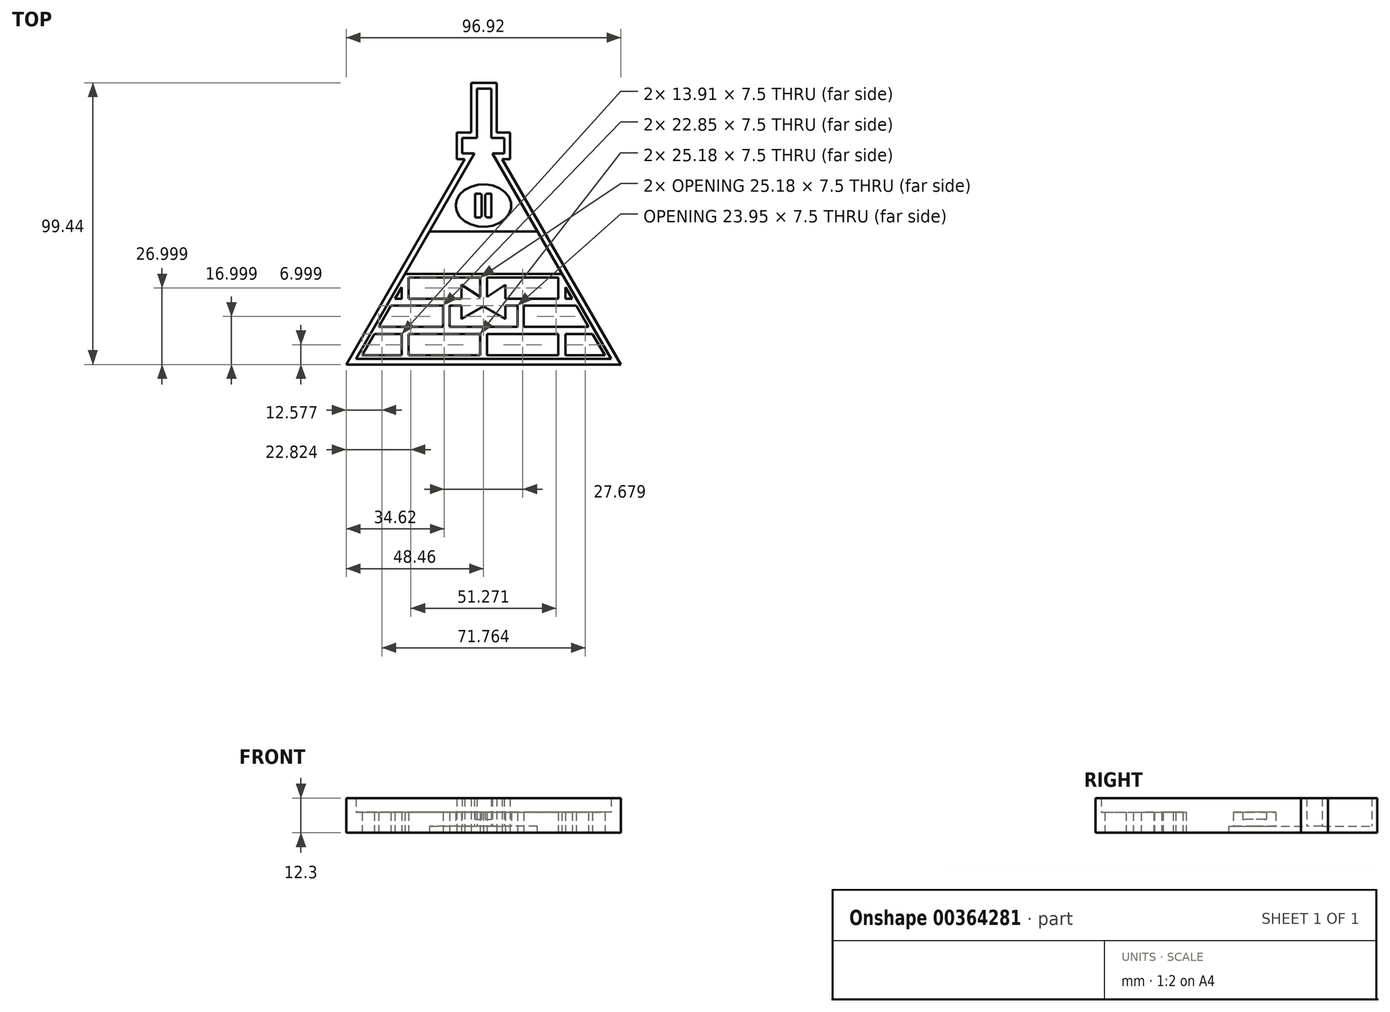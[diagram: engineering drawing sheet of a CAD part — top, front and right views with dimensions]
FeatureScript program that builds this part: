
annotation { "Feature Type Name" : "Feature", "Feature Type Description" : "" }
export const myFeature = defineFeature(function(context is Context, id is Id, definition is map)
    precondition{}
    {
        {
            var Q0;
            Q0=qCreatedBy(makeId("Top.planeOp"),FACE);
            var sketch = newSketch(context, id + "F0", { "sketchPlane" : qUnion([Q0])});
            skLineSegment(sketch, "E0", {"start": v(-13.53, -35.83) * mm, "end": v(31.47, -35.83) * mm});
            skLineSegment(sketch, "E1", {"start": v(31.47, -35.83) * mm, "end": v(-10.37, 36.64) * mm});
            skLineSegment(sketch, "E2", {"start": v(-13.53, 25.79) * mm, "end": v(-13.53, 10.79) * mm});
            skPoint(sketch, "E3.orphan", {"position": v(-58.53, -35.83) * mm});
            skEllipticalArc(sketch, "E4", {});
            skLineSegment(sketch, "E5", {"start": v(-13.53, -5.83) * mm, "end": v(14.15, -5.83) * mm});
            skLineSegment(sketch, "E6", {"start": v(-7.04, -15.83) * mm, "end": v(19.92, -15.83) * mm});
            skLineSegment(sketch, "E7", {"start": v(-13.53, -25.83) * mm, "end": v(25.7, -25.83) * mm});
            skLineSegment(sketch, "E8", {"start": v(14.15, -5.83) * mm, "end": v(14.15, -15.83) * mm});
            skLineSegment(sketch, "E9.trimOffspring", {"start": v(14.15, -25.83) * mm, "end": v(14.15, -35.83) * mm});
            skLineSegment(sketch, "E10", {"start": v(-0.57, -15.83) * mm, "end": v(-0.57, -25.83) * mm});
            skLineSegment(sketch, "E11", {"start": v(-12.28, -34.58) * mm, "end": v(-12.28, -27.08) * mm});
            skLineSegment(sketch, "E12", {"start": v(-12.28, -27.08) * mm, "end": v(12.9, -27.08) * mm});
            skLineSegment(sketch, "E13", {"start": v(12.9, -27.08) * mm, "end": v(12.9, -34.58) * mm});
            skLineSegment(sketch, "E14", {"start": v(12.9, -34.58) * mm, "end": v(-12.28, -34.58) * mm});
            skLineSegment(sketch, "E15", {"start": v(15.4, -34.58) * mm, "end": v(15.4, -27.08) * mm});
            skLineSegment(sketch, "E16", {"start": v(15.4, -27.08) * mm, "end": v(24.97, -27.08) * mm});
            skLineSegment(sketch, "E17", {"start": v(24.97, -27.08) * mm, "end": v(29.3, -34.58) * mm});
            skLineSegment(sketch, "E18", {"start": v(29.3, -34.58) * mm, "end": v(15.4, -34.58) * mm});
            skLineSegment(sketch, "E19", {"start": v(0.68, -24.58) * mm, "end": v(0.68, -17.08) * mm});
            skLineSegment(sketch, "E20", {"start": v(0.68, -17.08) * mm, "end": v(19.2, -17.08) * mm});
            skLineSegment(sketch, "E21", {"start": v(19.2, -17.08) * mm, "end": v(23.53, -24.58) * mm});
            skLineSegment(sketch, "E22", {"start": v(23.53, -24.58) * mm, "end": v(0.68, -24.58) * mm});
            skLineSegment(sketch, "E23", {"start": v(-1.56, -17.08) * mm, "end": v(-1.56, -24.58) * mm});
            skLineSegment(sketch, "E24", {"start": v(-12.28, -18) * mm, "end": v(-5.79, -21.75) * mm});
            skLineSegment(sketch, "E25", {"start": v(-5.79, -21.75) * mm, "end": v(-5.79, -17.08) * mm});
            skLineSegment(sketch, "E26", {"start": v(-5.79, -17.08) * mm, "end": v(-1.56, -17.08) * mm});
            skLineSegment(sketch, "E27", {"start": v(-12.28, -7.08) * mm, "end": v(-12.28, -14.01) * mm});
            skLineSegment(sketch, "E28", {"start": v(-12.28, -14.01) * mm, "end": v(-5.79, -9.6) * mm});
            skLineSegment(sketch, "E29", {"start": v(-5.79, -9.6) * mm, "end": v(-5.79, -14.58) * mm});
            skLineSegment(sketch, "E30", {"start": v(-5.79, -14.58) * mm, "end": v(12.9, -14.58) * mm});
            skLineSegment(sketch, "E31", {"start": v(12.9, -14.58) * mm, "end": v(12.9, -7.08) * mm});
            skLineSegment(sketch, "E32", {"start": v(12.9, -7.08) * mm, "end": v(-12.28, -7.08) * mm});
            skLineSegment(sketch, "E33", {"start": v(15.4, -14.58) * mm, "end": v(15.4, -10.5) * mm});
            skLineSegment(sketch, "E34", {"start": v(15.4, -10.5) * mm, "end": v(17.76, -14.58) * mm});
            skLineSegment(sketch, "E35", {"start": v(17.76, -14.58) * mm, "end": v(15.4, -14.58) * mm});
            skFitSpline(sketch, "E36.0", {"points": [v(-22.02, 19.44) * mm, v(-22.17, 18.29) * mm, v(-22.02, 17.13) * mm, v(-21.58, 16) * mm, v(-20.82, 14.92) * mm, v(-19.78, 13.95) * mm, v(-18.47, 13.13) * mm, v(-16.94, 12.5) * mm, v(-15.56, 12.19) * mm, v(-14.4, 12.06) * mm, v(-13.53, 12.03) * mm, v(-12.65, 12.06) * mm, v(-11.5, 12.19) * mm, v(-10.12, 12.5) * mm, v(-8.59, 13.13) * mm, v(-7.28, 13.95) * mm, v(-6.24, 14.92) * mm, v(-5.48, 16) * mm, v(-5.04, 17.13) * mm, v(-4.89, 18.29) * mm, v(-5.04, 19.44) * mm, v(-5.48, 20.56) * mm, v(-6.24, 21.65) * mm, v(-7.28, 22.62) * mm, v(-8.59, 23.44) * mm, v(-10.12, 24.06) * mm, v(-11.5, 24.38) * mm, v(-12.65, 24.51) * mm, v(-13.53, 24.55) * mm, v(-14.4, 24.51) * mm, v(-15.56, 24.38) * mm, v(-16.94, 24.06) * mm, v(-18.47, 23.44) * mm, v(-19.78, 22.62) * mm, v(-20.82, 21.65) * mm, v(-21.58, 20.56) * mm, v(-22.02, 19.44) * mm, v(-22.17, 18.29) * mm, v(-22.02, 17.13) * mm]});
            skEllipticalArc(sketch, "E37.MirrorCS", {});
            skLineSegment(sketch, "E38.MirrorCS", {"start": v(-58.53, -35.83) * mm, "end": v(-16.69, 36.64) * mm});
            skLineSegment(sketch, "E39.MirrorCS", {"start": v(-13.53, -5.83) * mm, "end": v(-41.21, -5.83) * mm});
            skLineSegment(sketch, "E40.MirrorCS", {"start": v(-39.96, -7.08) * mm, "end": v(-14.78, -7.08) * mm});
            skLineSegment(sketch, "E41.MirrorCS", {"start": v(-14.78, -7.08) * mm, "end": v(-14.78, -14.01) * mm});
            skLineSegment(sketch, "E42.MirrorCS", {"start": v(-14.78, -14.01) * mm, "end": v(-21.28, -9.6) * mm});
            skLineSegment(sketch, "E43.MirrorCS", {"start": v(-21.28, -17.08) * mm, "end": v(-25.5, -17.08) * mm});
            skLineSegment(sketch, "E44.MirrorCS", {"start": v(-21.28, -21.75) * mm, "end": v(-21.28, -17.08) * mm});
            skLineSegment(sketch, "E45.MirrorCS", {"start": v(-25.5, -17.08) * mm, "end": v(-25.5, -24.58) * mm});
            skLineSegment(sketch, "E46.MirrorCS", {"start": v(-14.78, -18) * mm, "end": v(-21.28, -21.75) * mm});
            skLineSegment(sketch, "E47.MirrorCS", {"start": v(-13.53, -25.83) * mm, "end": v(-52.76, -25.83) * mm});
            skLineSegment(sketch, "E48.MirrorCS", {"start": v(-27.74, -24.58) * mm, "end": v(-27.74, -17.08) * mm});
            skLineSegment(sketch, "E49.MirrorCS", {"start": v(-20.03, -15.83) * mm, "end": v(-46.98, -15.83) * mm});
            skLineSegment(sketch, "E50.MirrorCS", {"start": v(-26.5, -15.83) * mm, "end": v(-26.5, -25.83) * mm});
            skLineSegment(sketch, "E51.MirrorCS", {"start": v(-39.96, -14.58) * mm, "end": v(-39.96, -7.08) * mm});
            skLineSegment(sketch, "E52.MirrorCS", {"start": v(-46.26, -17.08) * mm, "end": v(-50.6, -24.58) * mm});
            skLineSegment(sketch, "E53.MirrorCS", {"start": v(-52.04, -27.08) * mm, "end": v(-56.37, -34.58) * mm});
            skLineSegment(sketch, "E54.MirrorCS", {"start": v(-13.53, -35.83) * mm, "end": v(-58.53, -35.83) * mm});
            skLineSegment(sketch, "E55.MirrorCS", {"start": v(-14.78, -34.58) * mm, "end": v(-14.78, -27.08) * mm});
            skLineSegment(sketch, "E56.MirrorCS", {"start": v(-14.78, -27.08) * mm, "end": v(-39.96, -27.08) * mm});
            skLineSegment(sketch, "E57.MirrorCS", {"start": v(-39.96, -34.58) * mm, "end": v(-14.78, -34.58) * mm});
            skLineSegment(sketch, "E58.MirrorCS", {"start": v(-39.96, -27.08) * mm, "end": v(-39.96, -34.58) * mm});
            skLineSegment(sketch, "E59.MirrorCS", {"start": v(-41.21, -25.83) * mm, "end": v(-41.21, -35.83) * mm});
            skLineSegment(sketch, "E60.MirrorCS", {"start": v(-42.46, -34.58) * mm, "end": v(-42.46, -27.08) * mm});
            skLineSegment(sketch, "E61.MirrorCS", {"start": v(-27.74, -17.08) * mm, "end": v(-46.26, -17.08) * mm});
            skLineSegment(sketch, "E62.MirrorCS", {"start": v(-50.6, -24.58) * mm, "end": v(-27.74, -24.58) * mm});
            skLineSegment(sketch, "E63.MirrorCS", {"start": v(-56.37, -34.58) * mm, "end": v(-42.46, -34.58) * mm});
            skLineSegment(sketch, "E64.MirrorCS", {"start": v(-42.46, -27.08) * mm, "end": v(-52.04, -27.08) * mm});
            skLineSegment(sketch, "E65.MirrorCS", {"start": v(-21.28, -14.58) * mm, "end": v(-39.96, -14.58) * mm});
            skLineSegment(sketch, "E66.MirrorCS", {"start": v(-41.21, -5.83) * mm, "end": v(-41.21, -15.83) * mm});
            skLineSegment(sketch, "E67.MirrorCS", {"start": v(-42.46, -10.5) * mm, "end": v(-44.82, -14.58) * mm});
            skLineSegment(sketch, "E68.MirrorCS", {"start": v(-42.46, -14.58) * mm, "end": v(-42.46, -10.5) * mm});
            skLineSegment(sketch, "E69.MirrorCS", {"start": v(-44.82, -14.58) * mm, "end": v(-42.46, -14.58) * mm});
            skLineSegment(sketch, "E70.MirrorCS", {"start": v(-21.28, -9.6) * mm, "end": v(-21.28, -14.58) * mm});
            skLineSegment(sketch, "E71.trimOffspring", {"start": v(-13.53, -5.83) * mm, "end": v(-13.53, -15.83) * mm});
            skLineSegment(sketch, "E72.trimOffspring", {"start": v(-13.53, -25.83) * mm, "end": v(-13.53, -35.83) * mm});
            skLineSegment(sketch, "E73", {"start": v(-25.5, -24.58) * mm, "end": v(-1.56, -24.58) * mm});
            skLineSegment(sketch, "E74", {"start": v(-12.28, -18) * mm, "end": v(-13.53, -17.27) * mm});
            skLineSegment(sketch, "E75", {"start": v(-13.53, -17.27) * mm, "end": v(-14.78, -18) * mm});
            skFitSpline(sketch, "E76.0", {"points": [v(-22.02, 19.44) * mm, v(-22.17, 18.29) * mm, v(-22.02, 17.13) * mm, v(-21.58, 16) * mm, v(-20.82, 14.92) * mm, v(-19.78, 13.95) * mm, v(-18.47, 13.13) * mm, v(-16.94, 12.5) * mm, v(-15.56, 12.19) * mm, v(-14.4, 12.06) * mm, v(-13.53, 12.03) * mm, v(-12.65, 12.06) * mm, v(-11.5, 12.19) * mm, v(-10.12, 12.5) * mm, v(-8.59, 13.13) * mm, v(-7.28, 13.95) * mm, v(-6.24, 14.92) * mm, v(-5.48, 16) * mm, v(-5.04, 17.13) * mm, v(-4.89, 18.29) * mm, v(-5.04, 19.44) * mm, v(-5.48, 20.56) * mm, v(-6.24, 21.65) * mm, v(-7.28, 22.62) * mm, v(-8.59, 23.44) * mm, v(-10.12, 24.06) * mm, v(-11.5, 24.38) * mm, v(-12.65, 24.51) * mm, v(-13.53, 24.55) * mm, v(-14.4, 24.51) * mm, v(-15.56, 24.38) * mm, v(-16.94, 24.06) * mm, v(-18.47, 23.44) * mm, v(-19.78, 22.62) * mm, v(-20.82, 21.65) * mm, v(-21.58, 20.56) * mm, v(-22.02, 19.44) * mm, v(-22.17, 18.29) * mm, v(-22.02, 17.13) * mm]});
            skLineSegment(sketch, "E77.bottom", {"start": v(-14.16, 23.29) * mm, "end": v(-12.9, 23.29) * mm});
            skLineSegment(sketch, "E77.top", {"start": v(-14.16, 13.29) * mm, "end": v(-12.9, 13.29) * mm});
            skLineSegment(sketch, "E77.left", {"start": v(-14.16, 23.29) * mm, "end": v(-14.16, 13.29) * mm});
            skLineSegment(sketch, "E77.right", {"start": v(-12.9, 23.29) * mm, "end": v(-12.9, 13.29) * mm});
            skPoint(sketch, "E78.middle", {"position": v(-13.53, 42.11) * mm});
            skLineSegment(sketch, "E79.top", {"start": v(-10.83, 59.61) * mm, "end": v(-15.83, 59.61) * mm});
            skLineSegment(sketch, "E79.left", {"start": v(-10.83, 42.11) * mm, "end": v(-10.83, 59.61) * mm});
            skLineSegment(sketch, "E79.right", {"start": v(-15.83, 42.11) * mm, "end": v(-15.83, 59.61) * mm});
            skLineSegment(sketch, "E80.bottom", {"start": v(-21.03, 42.11) * mm, "end": v(-15.83, 42.11) * mm});
            skLineSegment(sketch, "E80.top", {"start": v(-21.03, 36.64) * mm, "end": v(-16.69, 36.64) * mm});
            skLineSegment(sketch, "E80.left", {"start": v(-21.03, 42.11) * mm, "end": v(-21.03, 36.64) * mm});
            skLineSegment(sketch, "E80.right", {"start": v(-6.2, 42.11) * mm, "end": v(-6.2, 36.64) * mm});
            skLineSegment(sketch, "E81.trimOffspring", {"start": v(-10.83, 42.11) * mm, "end": v(-6.2, 42.11) * mm});
            skLineSegment(sketch, "E82.trimOffspring", {"start": v(-10.37, 36.64) * mm, "end": v(-6.2, 36.64) * mm});
            skLineSegment(sketch, "E83.0", {"start": v(-23.03, 44.11) * mm, "end": v(-17.83, 44.11) * mm});
            skLineSegment(sketch, "E83.1", {"start": v(-23.03, 44.11) * mm, "end": v(-23.03, 34.64) * mm});
            skLineSegment(sketch, "E83.2", {"start": v(-4.2, 44.11) * mm, "end": v(-4.2, 34.64) * mm});
            skLineSegment(sketch, "E83.3", {"start": v(-8.83, 44.11) * mm, "end": v(-4.2, 44.11) * mm});
            skLineSegment(sketch, "E83.4", {"start": v(-8.83, 44.11) * mm, "end": v(-8.83, 61.61) * mm});
            skLineSegment(sketch, "E83.5", {"start": v(-8.83, 61.61) * mm, "end": v(-17.83, 61.61) * mm});
            skLineSegment(sketch, "E83.6", {"start": v(-6.9, 34.64) * mm, "end": v(-4.2, 34.64) * mm});
            skLineSegment(sketch, "E83.7", {"start": v(34.93, -37.83) * mm, "end": v(-6.9, 34.64) * mm});
            skLineSegment(sketch, "E83.8", {"start": v(-17.83, 44.11) * mm, "end": v(-17.83, 61.61) * mm});
            skLineSegment(sketch, "E83.9", {"start": v(-13.53, -37.83) * mm, "end": v(34.93, -37.83) * mm});
            skLineSegment(sketch, "E83.10", {"start": v(-13.53, -37.83) * mm, "end": v(-62, -37.83) * mm});
            skLineSegment(sketch, "E83.11", {"start": v(-62, -37.83) * mm, "end": v(-20.15, 34.64) * mm});
            skLineSegment(sketch, "E83.12", {"start": v(-23.03, 34.64) * mm, "end": v(-20.15, 34.64) * mm});
            skLineSegment(sketch, "E84.bottom", {"start": v(-16.46, 22.5) * mm, "end": v(-14.16, 22.5) * mm});
            skLineSegment(sketch, "E84.top", {"start": v(-16.46, 14.12) * mm, "end": v(-14.16, 14.12) * mm});
            skLineSegment(sketch, "E84.left", {"start": v(-16.46, 22.5) * mm, "end": v(-16.46, 14.12) * mm});
            skLineSegment(sketch, "E84.right", {"start": v(-10.76, 22.5) * mm, "end": v(-10.76, 14.12) * mm});
            skLineSegment(sketch, "E85.trimOffspring", {"start": v(-12.9, 22.5) * mm, "end": v(-10.76, 22.5) * mm});
            skLineSegment(sketch, "E86.trimOffspring", {"start": v(-12.9, 14.12) * mm, "end": v(-10.76, 14.12) * mm});
            const initialGuessF0  = {"E4": [-0.013530587022128426, 0.018286398476100092, 0, 1, 0.0075, 0.009843170482444584, 3.141592653589793, 6.283185307179586], "E37.MirrorCS": [-0.013530587022128426, 0.018286398476100092, 0, 1, 0.0075, 0.009843170482444584, 6.283185307179586, 3.141592653589793]};
            skSetInitialGuess(sketch, initialGuessF0);
            skSolve(sketch);
        }
        {
            var Q0;
            {var subQ1=sQuery(id+"F0.wireOp",EDGE,"E4");Q0=makeQuery(id+"F0.imprint","IMPRINT",FACE,{"disambiguationData":[TD([[makeQuery(id+"F0.imprint","IMPRINT",EDGE,{"derivedFrom":subQ1}),1.0]])]});}
            var Q1;
            {var subQ0=sQuery(id+"F0.wireOp",EDGE,"E37.MirrorCS");Q1=makeQuery(id+"F0.imprint","IMPRINT",FACE,{"disambiguationData":[TD([[makeQuery(id+"F0.imprint","IMPRINT",EDGE,{"derivedFrom":subQ0}),1.0]])]});}
            var Q2;
            {var subQ5=sQuery(id+"F0.wireOp",EDGE,"E77.right");Q2=makeQuery(id+"F0.imprint","IMPRINT",FACE,{"disambiguationData":[TD([[makeQuery(id+"F0.imprint","IMPRINT",EDGE,{"derivedFrom":subQ5}),-1.0]])]});}
            var Q3;
            {var subQ5=sQuery(id+"F0.wireOp",EDGE,"E77.left");Q3=makeQuery(id+"F0.imprint","IMPRINT",FACE,{"disambiguationData":[TD([[makeQuery(id+"F0.imprint","IMPRINT",EDGE,{"derivedFrom":subQ5}),1.0]])]});}
            var Q4;
            Q4=makeQuery(id+"F0.imprint","IMPRINT",FACE,{"disambiguationData":[TD([[makeQuery(id+"F0.imprint","IMPRINT",EDGE,{"derivedFrom":sQuery(id+"F0.wireOp",EDGE,"E5")}),-1.0]])]});
            var Q5;
            {var subQ0=sQuery(id+"F0.wireOp",EDGE,"E66.MirrorCS");Q5=makeQuery(id+"F0.imprint","IMPRINT",FACE,{"disambiguationData":[TD([[makeQuery(id+"F0.imprint","IMPRINT",EDGE,{"derivedFrom":subQ0}),-1.0]])]});}
            var Q6;
            Q6=makeQuery(id+"F0.imprint","IMPRINT",FACE,{"disambiguationData":[TD([[makeQuery(id+"F0.imprint","IMPRINT",EDGE,{"derivedFrom":sQuery(id+"F0.wireOp",EDGE,"E48.MirrorCS")}),-1.0]])]});
            var Q7;
            Q7=makeQuery(id+"F0.imprint","IMPRINT",FACE,{"disambiguationData":[TD([[makeQuery(id+"F0.imprint","IMPRINT",EDGE,{"derivedFrom":sQuery(id+"F0.wireOp",EDGE,"E53.MirrorCS")}),-1.0]])]});
            var Q8;
            Q8=makeQuery(id+"F0.imprint","IMPRINT",FACE,{"disambiguationData":[TD([[makeQuery(id+"F0.imprint","IMPRINT",EDGE,{"derivedFrom":sQuery(id+"F0.wireOp",EDGE,"E55.MirrorCS")}),-1.0]])]});
            var Q9;
            {var subQ0=sQuery(id+"F0.wireOp",EDGE,"E9.trimOffspring");Q9=makeQuery(id+"F0.imprint","IMPRINT",FACE,{"disambiguationData":[TD([[makeQuery(id+"F0.imprint","IMPRINT",EDGE,{"derivedFrom":subQ0}),-1.0]])]});}
            var Q10;
            {var subQ2=sQuery(id+"F0.wireOp",EDGE,"E10");Q10=makeQuery(id+"F0.imprint","IMPRINT",FACE,{"disambiguationData":[TD([[makeQuery(id+"F0.imprint","IMPRINT",EDGE,{"derivedFrom":subQ2}),1.0]])]});}
            var Q11;
            {var subQ3=sQuery(id+"F0.wireOp",EDGE,"E8");Q11=makeQuery(id+"F0.imprint","IMPRINT",FACE,{"disambiguationData":[TD([[makeQuery(id+"F0.imprint","IMPRINT",EDGE,{"derivedFrom":subQ3}),1.0]])]});}
            var Q12;
            {var subQ0=sQuery(id+"F0.wireOp",EDGE,"E9.trimOffspring");Q12=makeQuery(id+"F0.imprint","IMPRINT",FACE,{"disambiguationData":[TD([[makeQuery(id+"F0.imprint","IMPRINT",EDGE,{"derivedFrom":subQ0}),1.0]])]});}
            var Q13;
            Q13=makeQuery(id+"F0.imprint","IMPRINT",FACE,{"disambiguationData":[TD([[makeQuery(id+"F0.imprint","IMPRINT",EDGE,{"derivedFrom":sQuery(id+"F0.wireOp",EDGE,"E79.top")}),-1.0]])]});
            extrude(context, id + "F1", {"entities" : qUnion([Q0, Q1, Q2, Q3, Q4, Q5, Q6, Q7, Q8, Q9, Q10, Q11, Q12, Q13]), "depth" : 5 * mm});
        }
        {
            var Q0;
            Q0=makeQuery(id+"F0.imprint","IMPRINT",FACE,{"disambiguationData":[TD([[makeQuery(id+"F0.imprint","IMPRINT",EDGE,{"derivedFrom":sQuery(id+"F0.wireOp",EDGE,"E79.top")}),-1.0]])]});
            var sketch = newSketch(context, id + "F2", { "sketchPlane" : qUnion([Q0])});
            skLineSegment(sketch, "E87.0", {"start": v(-8.83, 61.61) * mm, "end": v(-17.83, 61.61) * mm});
            skLineSegment(sketch, "E88.0", {"start": v(-8.83, 44.11) * mm, "end": v(-8.83, 61.61) * mm});
            skLineSegment(sketch, "E89.0", {"start": v(-17.83, 44.11) * mm, "end": v(-17.83, 61.61) * mm});
            skLineSegment(sketch, "E90.0", {"start": v(-23.03, 44.11) * mm, "end": v(-17.83, 44.11) * mm});
            skLineSegment(sketch, "E91.0", {"start": v(-23.03, 44.11) * mm, "end": v(-23.03, 34.64) * mm});
            skLineSegment(sketch, "E92.0", {"start": v(-23.03, 34.64) * mm, "end": v(-20.15, 34.64) * mm});
            skLineSegment(sketch, "E93.0", {"start": v(-62, -37.83) * mm, "end": v(-20.15, 34.64) * mm});
            skLineSegment(sketch, "E94.0", {"start": v(-8.83, 44.11) * mm, "end": v(-4.2, 44.11) * mm});
            skLineSegment(sketch, "E95.0", {"start": v(-4.2, 44.11) * mm, "end": v(-4.2, 34.64) * mm});
            skPoint(sketch, "E96.0", {"position": v(-5.56, 34.64) * mm});
            skLineSegment(sketch, "E97.0", {"start": v(-6.9, 34.64) * mm, "end": v(-4.2, 34.64) * mm});
            skLineSegment(sketch, "E98.0", {"start": v(34.93, -37.83) * mm, "end": v(-6.9, 34.64) * mm});
            skLineSegment(sketch, "E99.0", {"start": v(-13.53, -37.83) * mm, "end": v(-62, -37.83) * mm});
            skLineSegment(sketch, "E100.0", {"start": v(31.47, -35.83) * mm, "end": v(5.48, 9.19) * mm});
            skLineSegment(sketch, "E101.0", {"start": v(-58.53, -35.83) * mm, "end": v(-32.54, 9.19) * mm});
            skLineSegment(sketch, "E102.0.0", {"start": v(-13.53, -37.83) * mm, "end": v(34.93, -37.83) * mm});
            skLineSegment(sketch, "E102.0.3", {"start": v(-4.2, 34.64) * mm, "end": v(-4.2, 44.11) * mm});
            skLineSegment(sketch, "E102.0.4", {"start": v(-4.2, 44.11) * mm, "end": v(-8.83, 44.11) * mm});
            skLineSegment(sketch, "E102.0.7", {"start": v(-17.83, 61.61) * mm, "end": v(-17.83, 44.11) * mm});
            skLineSegment(sketch, "E102.0.8", {"start": v(-17.83, 44.11) * mm, "end": v(-23.03, 44.11) * mm});
            skLineSegment(sketch, "E102.0.11", {"start": v(-20.15, 34.64) * mm, "end": v(-62, -37.83) * mm});
            skLineSegment(sketch, "E102.0.12", {"start": v(-62, -37.83) * mm, "end": v(-13.53, -37.83) * mm});
            skLineSegment(sketch, "E103.0", {"start": v(-13.53, -35.83) * mm, "end": v(-58.53, -35.83) * mm});
            skLineSegment(sketch, "E104.0", {"start": v(-13.53, -35.83) * mm, "end": v(31.47, -35.83) * mm});
            skLineSegment(sketch, "E105", {"start": v(5.48, 9.19) * mm, "end": v(-32.54, 9.19) * mm});
            skPoint(sketch, "E106.orphan", {"position": v(-10.37, 36.64) * mm});
            skPoint(sketch, "E107.orphan", {"position": v(-16.69, 36.64) * mm});
            skPoint(sketch, "E108.0.start.orphan", {"position": v(-21.03, 36.64) * mm});
            skPoint(sketch, "E109.0.start.orphan", {"position": v(-21.03, 42.11) * mm});
            skPoint(sketch, "E110.0.end.orphan", {"position": v(-15.83, 42.11) * mm});
            skPoint(sketch, "E111.0.end.orphan", {"position": v(-15.83, 59.61) * mm});
            skSolve(sketch);
        }
        {
            var Q0;
            Q0=qSketchRegion(id+"F2",true);
            var Q1;
            Q1=makeQuery(id+"F0.imprint","IMPRINT",FACE,{"disambiguationData":[TD([[makeQuery(id+"F0.imprint","IMPRINT",EDGE,{"derivedFrom":sQuery(id+"F0.wireOp",EDGE,"E5")}),-1.0]])]});
            var Q2;
            Q2=makeQuery(id+"F0.imprint","IMPRINT",FACE,{"disambiguationData":[TD([[makeQuery(id+"F0.imprint","IMPRINT",EDGE,{"derivedFrom":sQuery(id+"F0.wireOp",EDGE,"E48.MirrorCS")}),-1.0]])]});
            var Q3;
            Q3=makeQuery(id+"F0.imprint","IMPRINT",FACE,{"disambiguationData":[TD([[makeQuery(id+"F0.imprint","IMPRINT",EDGE,{"derivedFrom":sQuery(id+"F0.wireOp",EDGE,"E55.MirrorCS")}),-1.0]])]});
            var Q4;
            Q4=makeQuery(id+"F0.imprint","IMPRINT",FACE,{"disambiguationData":[TD([[makeQuery(id+"F0.imprint","IMPRINT",EDGE,{"derivedFrom":sQuery(id+"F0.wireOp",EDGE,"E53.MirrorCS")}),-1.0]])]});
            var Q5;
            {var subQ0=sQuery(id+"F0.wireOp",EDGE,"E66.MirrorCS");Q5=makeQuery(id+"F0.imprint","IMPRINT",FACE,{"disambiguationData":[TD([[makeQuery(id+"F0.imprint","IMPRINT",EDGE,{"derivedFrom":subQ0}),-1.0]])]});}
            var Q6;
            {var subQ0=sQuery(id+"F0.wireOp",EDGE,"E9.trimOffspring");Q6=makeQuery(id+"F0.imprint","IMPRINT",FACE,{"disambiguationData":[TD([[makeQuery(id+"F0.imprint","IMPRINT",EDGE,{"derivedFrom":subQ0}),-1.0]])]});}
            var Q7;
            {var subQ0=sQuery(id+"F0.wireOp",EDGE,"E8");Q7=makeQuery(id+"F0.imprint","IMPRINT",FACE,{"disambiguationData":[TD([[makeQuery(id+"F0.imprint","IMPRINT",EDGE,{"derivedFrom":subQ0}),1.0]])]});}
            var Q8;
            {var subQ2=sQuery(id+"F0.wireOp",EDGE,"E10");Q8=makeQuery(id+"F0.imprint","IMPRINT",FACE,{"disambiguationData":[TD([[makeQuery(id+"F0.imprint","IMPRINT",EDGE,{"derivedFrom":subQ2}),1.0]])]});}
            var Q9;
            {var subQ0=sQuery(id+"F0.wireOp",EDGE,"E9.trimOffspring");Q9=makeQuery(id+"F0.imprint","IMPRINT",FACE,{"disambiguationData":[TD([[makeQuery(id+"F0.imprint","IMPRINT",EDGE,{"derivedFrom":subQ0}),1.0]])]});}
            extrude(context, id + "F3", {"entities" : qUnion([Q0, Q1, Q2, Q3, Q4, Q5, Q6, Q7, Q8, Q9]), "operationType" : NewBodyOperationType.ADD, "oppositeDirection" : true, "depth" : 2.3 * mm, "offsetDistance" : 25 * mm});
        }
        {
            var Q0;
            Q0=makeQuery(id+"F1.opExtrude","CAP_FACE",FACE,{"disambiguationData":[OSD([sQuery(id+"F0.wireOp",EDGE,"E1"),sQuery(id+"F0.wireOp",EDGE,"E5"),sQuery(id+"F0.wireOp",EDGE,"E11"),sQuery(id+"F0.wireOp",EDGE,"E12"),sQuery(id+"F0.wireOp",EDGE,"E13"),sQuery(id+"F0.wireOp",EDGE,"E14"),sQuery(id+"F0.wireOp",EDGE,"E15"),sQuery(id+"F0.wireOp",EDGE,"E16"),sQuery(id+"F0.wireOp",EDGE,"E17"),sQuery(id+"F0.wireOp",EDGE,"E18"),sQuery(id+"F0.wireOp",EDGE,"E19"),sQuery(id+"F0.wireOp",EDGE,"E20"),sQuery(id+"F0.wireOp",EDGE,"E21"),sQuery(id+"F0.wireOp",EDGE,"E22"),sQuery(id+"F0.wireOp",EDGE,"E23"),sQuery(id+"F0.wireOp",EDGE,"E24"),sQuery(id+"F0.wireOp",EDGE,"E25"),sQuery(id+"F0.wireOp",EDGE,"E26"),sQuery(id+"F0.wireOp",EDGE,"E27"),sQuery(id+"F0.wireOp",EDGE,"E28"),sQuery(id+"F0.wireOp",EDGE,"E29"),sQuery(id+"F0.wireOp",EDGE,"E30"),sQuery(id+"F0.wireOp",EDGE,"E31"),sQuery(id+"F0.wireOp",EDGE,"E32"),sQuery(id+"F0.wireOp",EDGE,"E33"),sQuery(id+"F0.wireOp",EDGE,"E34"),sQuery(id+"F0.wireOp",EDGE,"E35"),sQuery(id+"F0.wireOp",EDGE,"E38.MirrorCS"),sQuery(id+"F0.wireOp",EDGE,"E39.MirrorCS"),sQuery(id+"F0.wireOp",EDGE,"E43.MirrorCS"),sQuery(id+"F0.wireOp",EDGE,"E44.MirrorCS"),sQuery(id+"F0.wireOp",EDGE,"E45.MirrorCS"),sQuery(id+"F0.wireOp",EDGE,"E46.MirrorCS"),sQuery(id+"F0.wireOp",EDGE,"E48.MirrorCS"),sQuery(id+"F0.wireOp",EDGE,"E40.MirrorCS"),sQuery(id+"F0.wireOp",EDGE,"E41.MirrorCS"),sQuery(id+"F0.wireOp",EDGE,"E42.MirrorCS"),sQuery(id+"F0.wireOp",EDGE,"E52.MirrorCS"),sQuery(id+"F0.wireOp",EDGE,"E53.MirrorCS"),sQuery(id+"F0.wireOp",EDGE,"E55.MirrorCS"),sQuery(id+"F0.wireOp",EDGE,"E56.MirrorCS"),sQuery(id+"F0.wireOp",EDGE,"E57.MirrorCS"),sQuery(id+"F0.wireOp",EDGE,"E58.MirrorCS"),sQuery(id+"F0.wireOp",EDGE,"E60.MirrorCS"),sQuery(id+"F0.wireOp",EDGE,"E61.MirrorCS"),sQuery(id+"F0.wireOp",EDGE,"E62.MirrorCS"),sQuery(id+"F0.wireOp",EDGE,"E63.MirrorCS"),sQuery(id+"F0.wireOp",EDGE,"E64.MirrorCS"),sQuery(id+"F0.wireOp",EDGE,"E65.MirrorCS"),sQuery(id+"F0.wireOp",EDGE,"E51.MirrorCS"),sQuery(id+"F0.wireOp",EDGE,"E67.MirrorCS"),sQuery(id+"F0.wireOp",EDGE,"E68.MirrorCS"),sQuery(id+"F0.wireOp",EDGE,"E69.MirrorCS"),sQuery(id+"F0.wireOp",EDGE,"E70.MirrorCS"),sQuery(id+"F0.wireOp",EDGE,"E73"),sQuery(id+"F0.wireOp",EDGE,"E74"),sQuery(id+"F0.wireOp",EDGE,"E75"),sQuery(id+"F0.wireOp",EDGE,"E79.top"),sQuery(id+"F0.wireOp",EDGE,"E79.left"),sQuery(id+"F0.wireOp",EDGE,"E79.right"),sQuery(id+"F0.wireOp",EDGE,"E80.bottom"),sQuery(id+"F0.wireOp",EDGE,"E80.top"),sQuery(id+"F0.wireOp",EDGE,"E80.left"),sQuery(id+"F0.wireOp",EDGE,"E80.right"),sQuery(id+"F0.wireOp",EDGE,"E81.trimOffspring"),sQuery(id+"F0.wireOp",EDGE,"E82.trimOffspring"),sQuery(id+"F0.wireOp",EDGE,"E83.0"),sQuery(id+"F0.wireOp",EDGE,"E83.1"),sQuery(id+"F0.wireOp",EDGE,"E83.2"),sQuery(id+"F0.wireOp",EDGE,"E83.3"),sQuery(id+"F0.wireOp",EDGE,"E83.4"),sQuery(id+"F0.wireOp",EDGE,"E83.5"),sQuery(id+"F0.wireOp",EDGE,"E83.6"),sQuery(id+"F0.wireOp",EDGE,"E83.7"),sQuery(id+"F0.wireOp",EDGE,"E83.8"),sQuery(id+"F0.wireOp",EDGE,"E83.9"),sQuery(id+"F0.wireOp",EDGE,"E83.10"),sQuery(id+"F0.wireOp",EDGE,"E83.11"),sQuery(id+"F0.wireOp",EDGE,"E83.12")])],"isStart":false});
            var sketch = newSketch(context, id + "F4", { "sketchPlane" : qUnion([Q0])});
            skLineSegment(sketch, "E112.0", {"start": v(-58.53, -35.83) * mm, "end": v(-16.69, 36.64) * mm});
            skLineSegment(sketch, "E113.0", {"start": v(-21.03, 36.64) * mm, "end": v(-16.69, 36.64) * mm});
            skLineSegment(sketch, "E114.0", {"start": v(-21.03, 42.11) * mm, "end": v(-21.03, 36.64) * mm});
            skLineSegment(sketch, "E115.0", {"start": v(-21.03, 42.11) * mm, "end": v(-15.83, 42.11) * mm});
            skLineSegment(sketch, "E116.0", {"start": v(-15.83, 42.11) * mm, "end": v(-15.83, 59.61) * mm});
            skLineSegment(sketch, "E117.0.0", {"start": v(-62, -37.83) * mm, "end": v(34.93, -37.83) * mm});
            skLineSegment(sketch, "E117.0.1", {"start": v(34.93, -37.83) * mm, "end": v(-6.9, 34.64) * mm});
            skLineSegment(sketch, "E117.0.2", {"start": v(-6.9, 34.64) * mm, "end": v(-4.2, 34.64) * mm});
            skLineSegment(sketch, "E117.0.3", {"start": v(-4.2, 34.64) * mm, "end": v(-4.2, 44.11) * mm});
            skLineSegment(sketch, "E117.0.4", {"start": v(-4.2, 44.11) * mm, "end": v(-8.83, 44.11) * mm});
            skLineSegment(sketch, "E117.0.5", {"start": v(-8.83, 44.11) * mm, "end": v(-8.83, 61.61) * mm});
            skLineSegment(sketch, "E117.0.6", {"start": v(-8.83, 61.61) * mm, "end": v(-17.83, 61.61) * mm});
            skLineSegment(sketch, "E117.0.7", {"start": v(-17.83, 61.61) * mm, "end": v(-17.83, 44.11) * mm});
            skLineSegment(sketch, "E117.0.8", {"start": v(-17.83, 44.11) * mm, "end": v(-23.03, 44.11) * mm});
            skLineSegment(sketch, "E117.0.9", {"start": v(-23.03, 44.11) * mm, "end": v(-23.03, 34.64) * mm});
            skLineSegment(sketch, "E117.0.10", {"start": v(-23.03, 34.64) * mm, "end": v(-20.15, 34.64) * mm});
            skLineSegment(sketch, "E117.0.11", {"start": v(-20.15, 34.64) * mm, "end": v(-62, -37.83) * mm});
            skLineSegment(sketch, "E118.0", {"start": v(31.47, -35.83) * mm, "end": v(-10.37, 36.64) * mm});
            skLineSegment(sketch, "E119.0", {"start": v(-13.53, -35.83) * mm, "end": v(31.47, -35.83) * mm});
            skLineSegment(sketch, "E120.0", {"start": v(-13.53, -35.83) * mm, "end": v(-58.53, -35.83) * mm});
            skLineSegment(sketch, "E121.0", {"start": v(-10.37, 36.64) * mm, "end": v(-6.2, 36.64) * mm});
            skLineSegment(sketch, "E122.0", {"start": v(-6.2, 42.11) * mm, "end": v(-6.2, 36.64) * mm});
            skLineSegment(sketch, "E123.0", {"start": v(-10.83, 42.11) * mm, "end": v(-6.2, 42.11) * mm});
            skLineSegment(sketch, "E124.0", {"start": v(-10.83, 42.11) * mm, "end": v(-10.83, 59.61) * mm});
            skLineSegment(sketch, "E125.0", {"start": v(-10.83, 59.61) * mm, "end": v(-15.83, 59.61) * mm});
            skSolve(sketch);
        }
        {
            var Q0;
            Q0=qSketchRegion(id+"F4",true);
            extrude(context, id + "F5", {"entities" : qUnion([Q0]), "operationType" : NewBodyOperationType.ADD, "depth" : 5 * mm});
        }
        {
            var Q0;
            {var subQ0=sQuery(id+"F0.wireOp",EDGE,"E84.bottom");Q0=makeQuery(id+"F0.imprint","IMPRINT",FACE,{"disambiguationData":[TD([[makeQuery(id+"F0.imprint","IMPRINT",EDGE,{"derivedFrom":subQ0}),-1.0]])]});}
            var Q1;
            Q1=makeQuery(id+"F0.imprint","IMPRINT",FACE,{"disambiguationData":[TD([[makeQuery(id+"F0.imprint","IMPRINT",EDGE,{"derivedFrom":sQuery(id+"F0.wireOp",EDGE,"E84.right")}),-1.0]])]});
            extrude(context, id + "F6", {"entities" : qUnion([Q0, Q1]), "operationType" : NewBodyOperationType.ADD, "depth" : 2.5 * mm});
        }
        {
            var Q0;
            Q0=makeQuery(id+"F1.opExtrude","SWEPT_EDGE",EDGE,{"disambiguationData":[OSD([sQuery(id+"F0.wireOp",EDGE,"E77.bottom"),sQuery(id+"F0.wireOp",EDGE,"E77.left")])]});
            var Q1;
            Q1=makeQuery(id+"F1.opExtrude","SWEPT_EDGE",EDGE,{"disambiguationData":[OSD([sQuery(id+"F0.wireOp",EDGE,"E77.bottom"),sQuery(id+"F0.wireOp",EDGE,"E77.right")])]});
            var Q2;
            Q2=makeQuery(id+"F1.opExtrude","SWEPT_EDGE",EDGE,{"disambiguationData":[OSD([sQuery(id+"F0.wireOp",EDGE,"E77.top"),sQuery(id+"F0.wireOp",EDGE,"E77.right")])]});
            var Q3;
            Q3=makeQuery(id+"F1.opExtrude","SWEPT_EDGE",EDGE,{"disambiguationData":[OSD([sQuery(id+"F0.wireOp",EDGE,"E77.top"),sQuery(id+"F0.wireOp",EDGE,"E77.left")])]});
            var Q4;
            Q4=makeQuery(id+"F6.opExtrude","CAP_EDGE",EDGE,{"disambiguationData":[OSD([sQuery(id+"F0.wireOp",EDGE,"E84.left")])],"isStart":false});
            var Q5;
            Q5=makeQuery(id+"F6.opExtrude","CAP_EDGE",EDGE,{"disambiguationData":[OSD([sQuery(id+"F0.wireOp",EDGE,"E84.right")])],"isStart":false});
            fillet(context, id + "F7", {"entities" : qUnion([Q0, Q1, Q2, Q3, Q4, Q5]), "radius" : 0.77 * mm, "tangentPropagation" : true, "allowEdgeOverflow" : false});
        }
    });
